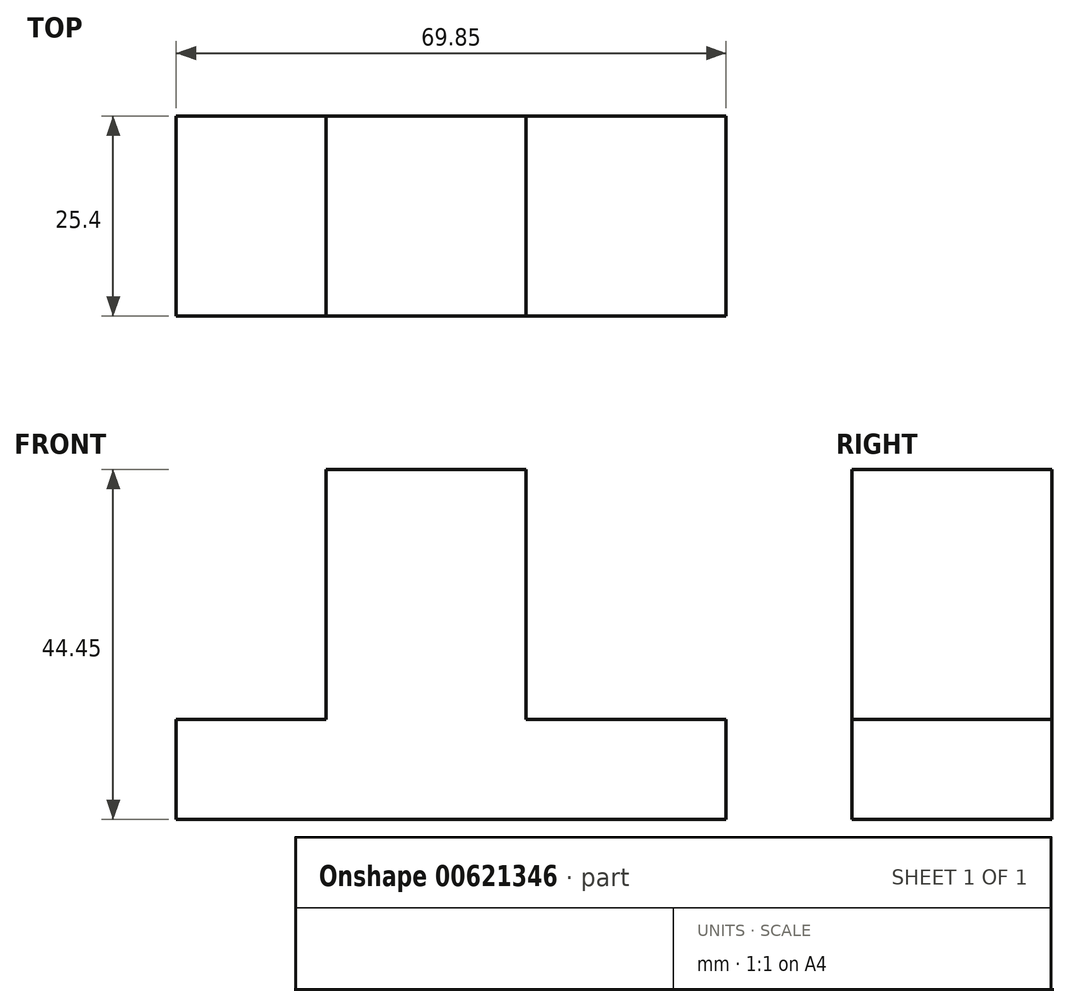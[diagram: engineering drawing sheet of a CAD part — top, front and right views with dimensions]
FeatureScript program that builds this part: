
annotation { "Feature Type Name" : "Feature", "Feature Type Description" : "" }
export const myFeature = defineFeature(function(context is Context, id is Id, definition is map)
    precondition{}
    {
        {
            var Q0;
            Q0=qCreatedBy(makeId("Front.planeOp"),FACE);
            var sketch = newSketch(context, id + "F0", { "sketchPlane" : qUnion([Q0])});
            skLineSegment(sketch, "E0", {"start": v(0, 0) * mm, "end": v(0, 44.45) * mm});
            skLineSegment(sketch, "E1", {"start": v(0, 44.45) * mm, "end": v(69.85, 44.45) * mm});
            skLineSegment(sketch, "E2", {"start": v(69.85, 44.45) * mm, "end": v(69.85, 0) * mm});
            skLineSegment(sketch, "E3", {"start": v(69.85, 0) * mm, "end": v(0, 0) * mm});
            skSolve(sketch);
        }
        {
            var Q0;
            Q0=makeQuery(id+"F0.imprint","IMPRINT",FACE,{"disambiguationData":[TD([[makeQuery(id+"F0.imprint","IMPRINT",EDGE,{"derivedFrom":sQuery(id+"F0.wireOp",EDGE,"E0")}),-1.0]])]});
            extrude(context, id + "F1", {"entities" : qUnion([Q0]), "depth" : 25.4 * mm, "offsetDistance" : 25.4 * mm});
        }
        {
            var Q0;
            Q0=makeQuery(id+"F1.opExtrude","CAP_FACE",FACE,{"disambiguationData":[OSD([sQuery(id+"F0.wireOp",EDGE,"E0"),sQuery(id+"F0.wireOp",EDGE,"E1"),sQuery(id+"F0.wireOp",EDGE,"E2"),sQuery(id+"F0.wireOp",EDGE,"E3")])],"isStart":false});
            var sketch = newSketch(context, id + "F2", { "sketchPlane" : qUnion([Q0])});
            skLineSegment(sketch, "E4", {"start": v(0, 0) * mm, "end": v(0, 12.7) * mm});
            skLineSegment(sketch, "E5", {"start": v(0, 12.7) * mm, "end": v(19.05, 12.7) * mm});
            skLineSegment(sketch, "E6", {"start": v(19.05, 12.7) * mm, "end": v(19.05, 44.45) * mm});
            skLineSegment(sketch, "E7", {"start": v(19.05, 44.45) * mm, "end": v(44.45, 44.45) * mm});
            skLineSegment(sketch, "E8", {"start": v(44.45, 44.45) * mm, "end": v(44.45, 12.7) * mm});
            skLineSegment(sketch, "E9", {"start": v(44.45, 12.7) * mm, "end": v(69.85, 12.7) * mm});
            skSolve(sketch);
        }
        {
            var Q0;
            {var subQ0=sQuery(id+"F2.wireOp",EDGE,"E5");Q0=makeQuery(id+"F2.imprint","IMPRINT",FACE,{"disambiguationData":[TD([[makeQuery(id+"F2.imprint","IMPRINT",EDGE,{"derivedFrom":subQ0}),1.0]])]});}
            var Q1;
            {var subQ0=sQuery(id+"F2.wireOp",EDGE,"E8");Q1=makeQuery(id+"F2.imprint","IMPRINT",FACE,{"disambiguationData":[TD([[makeQuery(id+"F2.imprint","IMPRINT",EDGE,{"derivedFrom":subQ0}),1.0]])]});}
            extrude(context, id + "F3", {"entities" : qUnion([Q0, Q1]), "operationType" : NewBodyOperationType.REMOVE, "oppositeDirection" : true, "depth" : 25.4 * mm, "offsetDistance" : 25.4 * mm});
        }
    });
